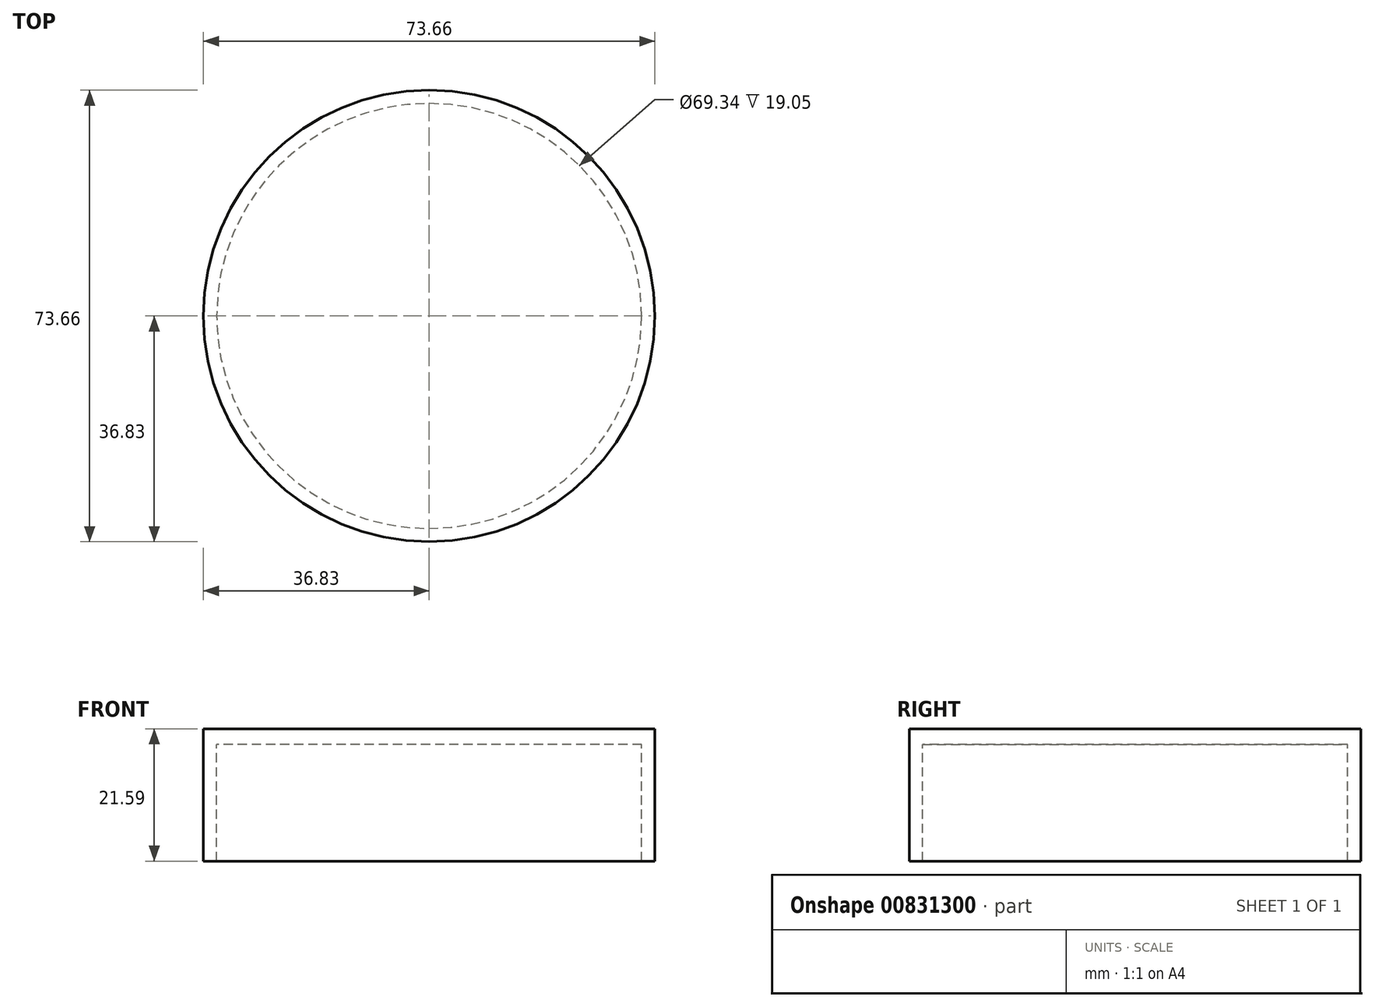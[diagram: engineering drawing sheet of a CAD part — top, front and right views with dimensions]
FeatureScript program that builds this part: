
annotation { "Feature Type Name" : "Feature", "Feature Type Description" : "" }
export const myFeature = defineFeature(function(context is Context, id is Id, definition is map)
    precondition{}
    {
        {
            var Q0;
            Q0=qCreatedBy(makeId("Top.planeOp"),FACE);
            var sketch = newSketch(context, id + "F0", { "sketchPlane" : qUnion([Q0])});
            skCircle(sketch, "E0", {"center": v(0, 0) * mm, "radius": 36.83 * mm});
            skSolve(sketch);
        }
        {
            var Q0;
            Q0=makeQuery(id+"F0.imprint","IMPRINT",FACE,{"disambiguationData":[TD([[makeQuery(id+"F0.imprint","IMPRINT",EDGE,{"derivedFrom":sQuery(id+"F0.wireOp",EDGE,"E0")}),1.0]])]});
            extrude(context, id + "F1", {"entities" : qUnion([Q0]), "depth" : 19.05 * mm, "offsetDistance" : 25.4 * mm});
        }
        {
            var Q0;
            Q0=makeQuery(id+"F1.opExtrude","CAP_FACE",FACE,{"disambiguationData":[OSD([sQuery(id+"F0.wireOp",EDGE,"E0")])],"isStart":false});
            var sketch = newSketch(context, id + "F2", { "sketchPlane" : qUnion([Q0])});
            skCircle(sketch, "E1", {"center": v(0, 0) * mm, "radius": 34.67 * mm});
            skSolve(sketch);
        }
        {
            var Q0;
            Q0=makeQuery(id+"F2.imprint","IMPRINT",FACE,{"disambiguationData":[TD([[makeQuery(id+"F2.imprint","IMPRINT",EDGE,{"derivedFrom":sQuery(id+"F2.wireOp",EDGE,"E1")}),1.0]])]});
            extrude(context, id + "F3", {"entities" : qUnion([Q0]), "operationType" : NewBodyOperationType.REMOVE, "oppositeDirection" : true, "depth" : 97.8 * mm, "offsetDistance" : 25.4 * mm});
        }
        {
            var Q0;
            Q0=makeQuery(id+"F1.opExtrude","CAP_FACE",FACE,{"disambiguationData":[OSD([sQuery(id+"F0.wireOp",EDGE,"E0")])],"isStart":false});
            var sketch = newSketch(context, id + "F4", { "sketchPlane" : qUnion([Q0])});
            skCircle(sketch, "E2", {"center": v(0, 0) * mm, "radius": 36.83 * mm});
            skSolve(sketch);
        }
        {
            var Q0;
            Q0=qSketchRegion(id+"F4",true);
            extrude(context, id + "F5", {"entities" : qUnion([Q0]), "operationType" : NewBodyOperationType.ADD, "depth" : 2.54 * mm, "offsetDistance" : 25.4 * mm});
        }
    });
